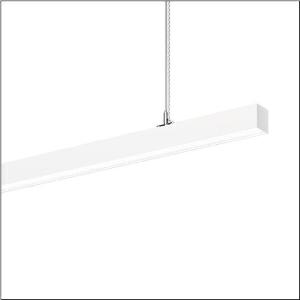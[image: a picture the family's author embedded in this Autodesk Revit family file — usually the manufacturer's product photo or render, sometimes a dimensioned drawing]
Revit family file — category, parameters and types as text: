
# Revit family: silica_r__21_51mx30tat4w_7b2a
name_source: partatom
category: Lighting Fixtures
units: mm (PartAtom-declared; Revit-internal decimal feet)

## family parameters
Cut with Voids When Loaded = No
Host = Face
Light Source = No
Part Type = Normal
Room Calculation Point = No
Round Connector Dimension = Use Diameter
Shared = No

## types (1)
- --- (1 x LED, 4120 lm, 33.8 W, 6500K)
    Apparent Load = 34 VA
    CIE Flux Codes = 47 79 96 58 100
    Color Rendering = 80
    Color Temperature = 6500K
    Default Elevation = 1800 mm
    Description = Silica® 21, office luminaire, primary optical cover: cover, of PMMA, opal, light emission: direct/indirect distribution, primary light characteristic: symmetric, installation type: suspended mounting, LED, rated luminous flux: 4.120lm, luminous efficacy: 116lm/W, light colour: 8tw, colour temperature: 2700..6500K, control gear: ECG DALI, with terminal, 3+2-pole, max. 2.5mm², mains connection: 220..240V, AC, 50/60Hz, rated input power: 35.5W, luminaire housing, of aluminium, traffic white (RAL 9016), length: 1.204mm, width: 53mm, height: 53mm, protection rating (complete): IP20, insulation class (complete): insulation class I (protective earthing), certification: CE, permissible operating ambient temperature: 0..+35°C, standard: EN 50419, packaging unit: 1 piece
    Height = 53 mm
    Lamp = 1 x LED
    Lamp Light Flux = 4120 lm
    Lamp Power = 33.8 W
    Lamp count = 1
    Length = 1204 mm
    Luminous efficacy = 122 lm/W
    Manufacturer = Siteco
    ModVariant = No
    Model = 51MX30TAT4W
    Mounting Place = Ceiling
    Mounting Type = Pendant
    Number of Poles = 1
    OnlyDefault = Yes
    Power Factor = 1
    Product Name = Silica® 21
    Product group = office luminaire | ceiling pendant
    ProductGroupID = 902
    Protection Class = Protection class I
    Protection Degree = IP 20
    RLX_Detail_Level = 1
    RLX_Emergency_Light_Flux = 0 lm
    RLX_Emergency_Type = 0
    RLX_Emergency_Type_DB = No
    RlxData = <blob elided: 18133 chars, md5=78fb80a3>
    Socket = socket
    Standby Power = 0 W
    System Light Flux = 4120 lm
    System Power = 34 W
    Type Comments = individual setting
    Type Image = l_1335916.jpg
    URL = http://relux.com
    VarID = @adj_109459
    Voltage = 0 V
    Weight = 0.00 kg
    Width = 53 mm

## geometry (parser evidence)
native form markers: Blend x4, Sweep x13
no freeform markers — native parametric forms only
